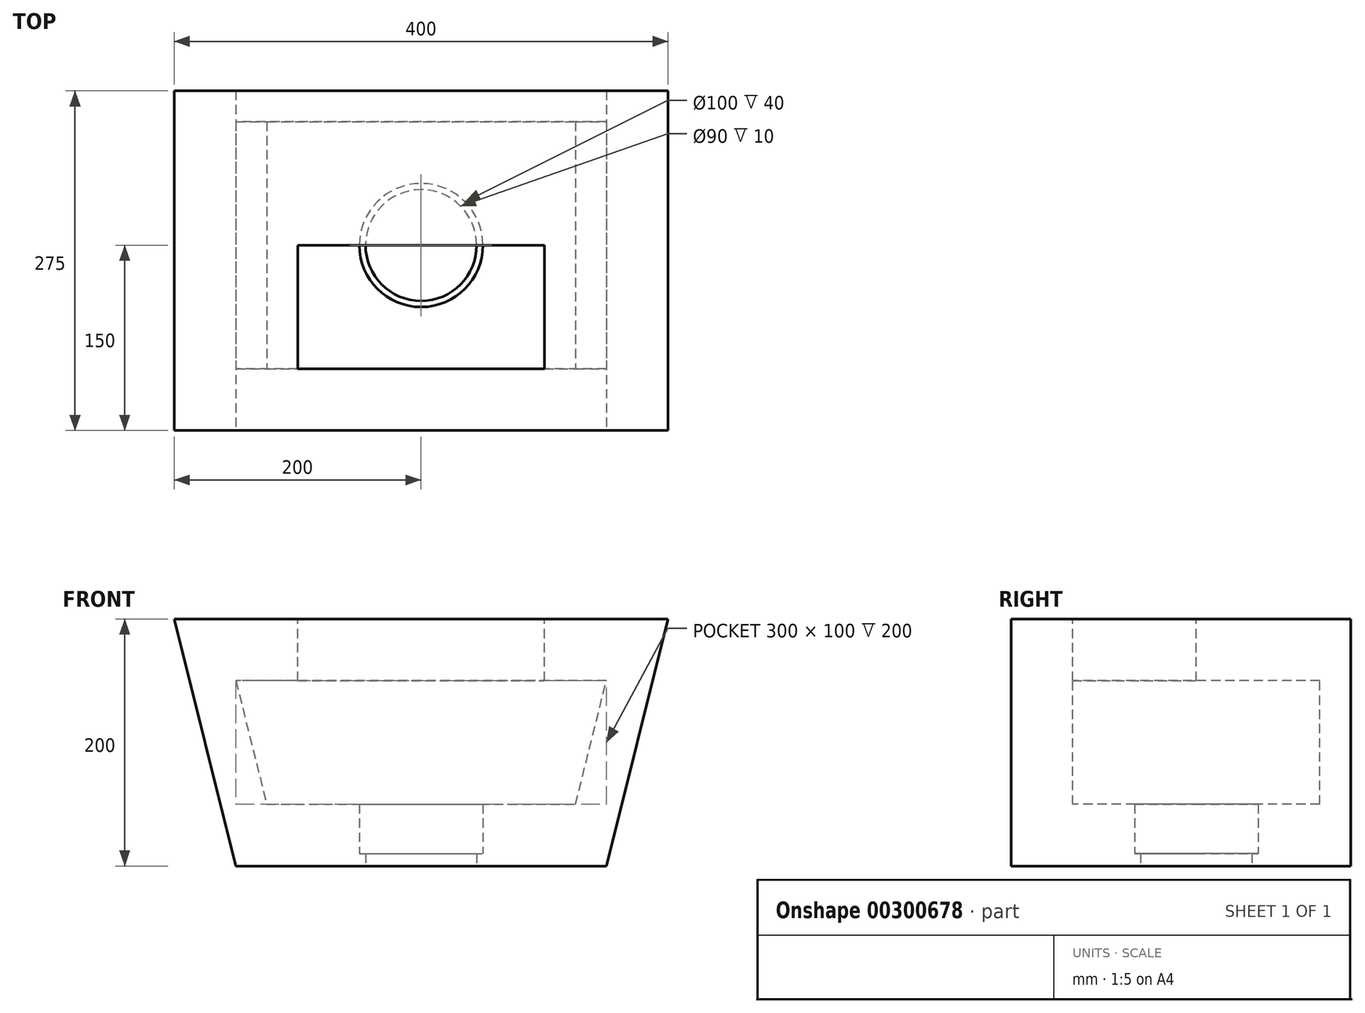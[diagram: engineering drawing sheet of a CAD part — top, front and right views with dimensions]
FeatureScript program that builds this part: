
annotation { "Feature Type Name" : "Feature", "Feature Type Description" : "" }
export const myFeature = defineFeature(function(context is Context, id is Id, definition is map)
    precondition{}
    {
        {
            var Q0;
            Q0=qCreatedBy(makeId("Front.planeOp"),FACE);
            var sketch = newSketch(context, id + "F0", { "sketchPlane" : qUnion([Q0])});
            skLineSegment(sketch, "E0.top", {"start": v(150, 50) * mm, "end": v(-150, 50) * mm});
            skPoint(sketch, "E0.middle", {"position": v(0, 0) * mm});
            skLineSegment(sketch, "E1", {"start": v(-150, 50) * mm, "end": v(-125, -50) * mm});
            skLineSegment(sketch, "E2", {"start": v(125, -50) * mm, "end": v(150, 50) * mm});
            skLineSegment(sketch, "E3", {"start": v(-125, -50) * mm, "end": v(125, -50) * mm});
            skLineSegment(sketch, "E4.top", {"start": v(200, 100) * mm, "end": v(-200, 100) * mm});
            skLineSegment(sketch, "E5", {"start": v(-200, 100) * mm, "end": v(-150, -100) * mm});
            skLineSegment(sketch, "E6", {"start": v(200, 100) * mm, "end": v(150, -100) * mm});
            skLineSegment(sketch, "E7", {"start": v(-150, -100) * mm, "end": v(150, -100) * mm});
            skLineSegment(sketch, "E8", {"start": v(0, 0) * mm, "end": v(-175, 0) * mm});
            skLineSegment(sketch, "E9", {"start": v(-175, 0) * mm, "end": v(0, 0) * mm});
            skLineSegment(sketch, "E10", {"start": v(175, 0) * mm, "end": v(0, 0) * mm});
            skSolve(sketch);
        }
        {
            var Q0;
            {var subQ1=sQuery(id+"F0.wireOp",EDGE,"E0.top");Q0=makeQuery(id+"F0.imprint","IMPRINT",FACE,{"disambiguationData":[TD([[makeQuery(id+"F0.imprint","IMPRINT",EDGE,{"derivedFrom":subQ1}),-1.0]])]});}
            var Q1;
            {var subQ0=sQuery(id+"F0.wireOp",EDGE,"E3");Q1=makeQuery(id+"F0.imprint","IMPRINT",FACE,{"disambiguationData":[TD([[makeQuery(id+"F0.imprint","IMPRINT",EDGE,{"derivedFrom":subQ0}),-1.0]])]});}
            extrude(context, id + "F1", {"entities" : qUnion([Q0, Q1]), "oppositeDirection" : true, "depth" : 200 * mm});
        }
        {
            var Q0;
            Q0=makeQuery(id+"F1.opExtrude","SWEPT_FACE",FACE,{"disambiguationData":[OSD([sQuery(id+"F0.wireOp",EDGE,"E7")])]});
            var sketch = newSketch(context, id + "F2", { "sketchPlane" : qUnion([Q0])});
            skPoint(sketch, "E11.endSnap0", {"position": v(0, 0) * mm});
            skCircle(sketch, "E12", {"center": v(0, -100) * mm, "radius": 50 * mm});
            skSolve(sketch);
        }
        {
            var Q0;
            Q0=makeQuery(id+"F2.imprint","IMPRINT",FACE,{"disambiguationData":[TD([[makeQuery(id+"F2.imprint","IMPRINT",EDGE,{"derivedFrom":sQuery(id+"F2.wireOp",EDGE,"E12")}),1.0]])]});
            extrude(context, id + "F3", {"entities" : qUnion([Q0]), "operationType" : NewBodyOperationType.REMOVE, "oppositeDirection" : true, "depth" : 50 * mm});
        }
        {
            var Q0;
            Q0=makeQuery(id+"F1.opExtrude","SWEPT_FACE",FACE,{"disambiguationData":[OSD([sQuery(id+"F0.wireOp",EDGE,"E7")])]});
            var sketch = newSketch(context, id + "F4", { "sketchPlane" : qUnion([Q0])});
            skLineSegment(sketch, "E13", {"start": v(0, 0) * mm, "end": v(0, -100) * mm});
            skCircle(sketch, "E14", {"center": v(0, -100) * mm, "radius": 45 * mm});
            skSolve(sketch);
        }
        {
            var Q0;
            Q0=makeQuery(id+"F4.imprint","IMPRINT",FACE,{"disambiguationData":[TD([[makeQuery(id+"F4.imprint","IMPRINT",EDGE,{"derivedFrom":sQuery(id+"F4.wireOp",EDGE,"E14")}),-1.0]])]});
            extrude(context, id + "F5", {"entities" : qUnion([Q0]), "operationType" : NewBodyOperationType.ADD, "oppositeDirection" : true, "depth" : 10 * mm});
        }
        {
            var Q0;
            Q0=makeQuery(id+"F1.opExtrude","CAP_FACE",FACE,{"disambiguationData":[OSD([sQuery(id+"F0.wireOp",EDGE,"E0.top"),sQuery(id+"F0.wireOp",EDGE,"E1"),sQuery(id+"F0.wireOp",EDGE,"E2"),sQuery(id+"F0.wireOp",EDGE,"E3"),sQuery(id+"F0.wireOp",EDGE,"E4.top"),sQuery(id+"F0.wireOp",EDGE,"E5"),sQuery(id+"F0.wireOp",EDGE,"E6"),sQuery(id+"F0.wireOp",EDGE,"E7")])],"isStart":true});
            var sketch = newSketch(context, id + "F6", { "sketchPlane" : qUnion([Q0])});
            skLineSegment(sketch, "E15", {"start": v(200, 100) * mm, "end": v(150, -100) * mm});
            skLineSegment(sketch, "E16", {"start": v(150, -100) * mm, "end": v(-150, -100) * mm});
            skLineSegment(sketch, "E17", {"start": v(-200, 100) * mm, "end": v(-150, -100) * mm});
            skLineSegment(sketch, "E18", {"start": v(-200, 100) * mm, "end": v(200, 100) * mm});
            skSolve(sketch);
        }
        {
            var Q0;
            Q0=makeQuery(id+"F6.imprint","IMPRINT",FACE,{"disambiguationData":[TD([[makeQuery(id+"F6.imprint","IMPRINT",EDGE,{"derivedFrom":sQuery(id+"F6.wireOp",EDGE,"E15")}),-1.0]])]});
            var Q1;
            Q1=makeQuery(id+"F6.imprint","IMPRINT",FACE,{"disambiguationData":[TD([[makeQuery(id+"F6.imprint","IMPRINT",EDGE,{"derivedFrom":makeQuery(id+"F1.opExtrude","CAP_EDGE",EDGE,{"disambiguationData":[OSD([sQuery(id+"F0.wireOp",EDGE,"E0.top")])],"isStart":true})}),1.0]])]});
            extrude(context, id + "F7", {"entities" : qUnion([Q0, Q1]), "operationType" : NewBodyOperationType.ADD, "depth" : 50 * mm});
        }
        {
            var Q0;
            Q0=makeQuery(id+"F1.opExtrude","CAP_FACE",FACE,{"disambiguationData":[OSD([sQuery(id+"F0.wireOp",EDGE,"E0.top"),sQuery(id+"F0.wireOp",EDGE,"E1"),sQuery(id+"F0.wireOp",EDGE,"E2"),sQuery(id+"F0.wireOp",EDGE,"E3"),sQuery(id+"F0.wireOp",EDGE,"E4.top"),sQuery(id+"F0.wireOp",EDGE,"E5"),sQuery(id+"F0.wireOp",EDGE,"E6"),sQuery(id+"F0.wireOp",EDGE,"E7")])],"isStart":false});
            var sketch = newSketch(context, id + "F8", { "sketchPlane" : qUnion([Q0])});
            skLineSegment(sketch, "E19", {"start": v(200, 100) * mm, "end": v(150, -100) * mm});
            skLineSegment(sketch, "E20", {"start": v(150, -100) * mm, "end": v(-150, -100) * mm});
            skLineSegment(sketch, "E21", {"start": v(-200, 100) * mm, "end": v(200, 100) * mm});
            skLineSegment(sketch, "E22", {"start": v(-150, -100) * mm, "end": v(-200, 100) * mm});
            skSolve(sketch);
        }
        {
            var Q0;
            Q0=makeQuery(id+"F8.imprint","IMPRINT",FACE,{"disambiguationData":[TD([[makeQuery(id+"F8.imprint","IMPRINT",EDGE,{"derivedFrom":sQuery(id+"F8.wireOp",EDGE,"E19")}),-1.0]])]});
            var Q1;
            Q1=makeQuery(id+"F8.imprint","IMPRINT",FACE,{"disambiguationData":[TD([[makeQuery(id+"F8.imprint","IMPRINT",EDGE,{"derivedFrom":makeQuery(id+"F1.opExtrude","CAP_EDGE",EDGE,{"disambiguationData":[OSD([sQuery(id+"F0.wireOp",EDGE,"E0.top")])],"isStart":false})}),-1.0]])]});
            extrude(context, id + "F9", {"entities" : qUnion([Q0, Q1]), "operationType" : NewBodyOperationType.ADD, "depth" : 25 * mm});
        }
        {
            var Q0;
            Q0=makeQuery(id+"F9.boolean.opBoolean","MERGE",FACE,{"derivedFrom":[makeQuery(id+"F7.boolean.opBoolean","MERGE",FACE,{"derivedFrom":[makeQuery(id+"F1.opExtrude","SWEPT_FACE",FACE,{"disambiguationData":[OSD([sQuery(id+"F0.wireOp",EDGE,"E4.top")])]}),makeQuery(id+"F7.opExtrude","SWEPT_FACE",FACE,{"disambiguationData":[OSD([sQuery(id+"F6.wireOp",EDGE,"E18")])]})]}),makeQuery(id+"F9.opExtrude","SWEPT_FACE",FACE,{"disambiguationData":[OSD([sQuery(id+"F8.wireOp",EDGE,"E21")])]})]});
            var sketch = newSketch(context, id + "F10", { "sketchPlane" : qUnion([Q0])});
            skLineSegment(sketch, "E23.top", {"start": v(-100, 100) * mm, "end": v(100, 100) * mm});
            skLineSegment(sketch, "E23.left", {"start": v(-100, 0) * mm, "end": v(-100, 100) * mm});
            skLineSegment(sketch, "E23.right", {"start": v(100, 0) * mm, "end": v(100, 100) * mm});
            skLineSegment(sketch, "E24", {"start": v(-100, 0) * mm, "end": v(100, 0) * mm});
            skSolve(sketch);
        }
        {
            var Q0;
            Q0=makeQuery(id+"F10.imprint","IMPRINT",FACE,{"disambiguationData":[TD([[makeQuery(id+"F10.imprint","IMPRINT",EDGE,{"derivedFrom":sQuery(id+"F10.wireOp",EDGE,"E23.top")}),-1.0]])]});
            extrude(context, id + "F11", {"entities" : qUnion([Q0]), "operationType" : NewBodyOperationType.REMOVE, "oppositeDirection" : true, "depth" : 50 * mm});
        }
    });
